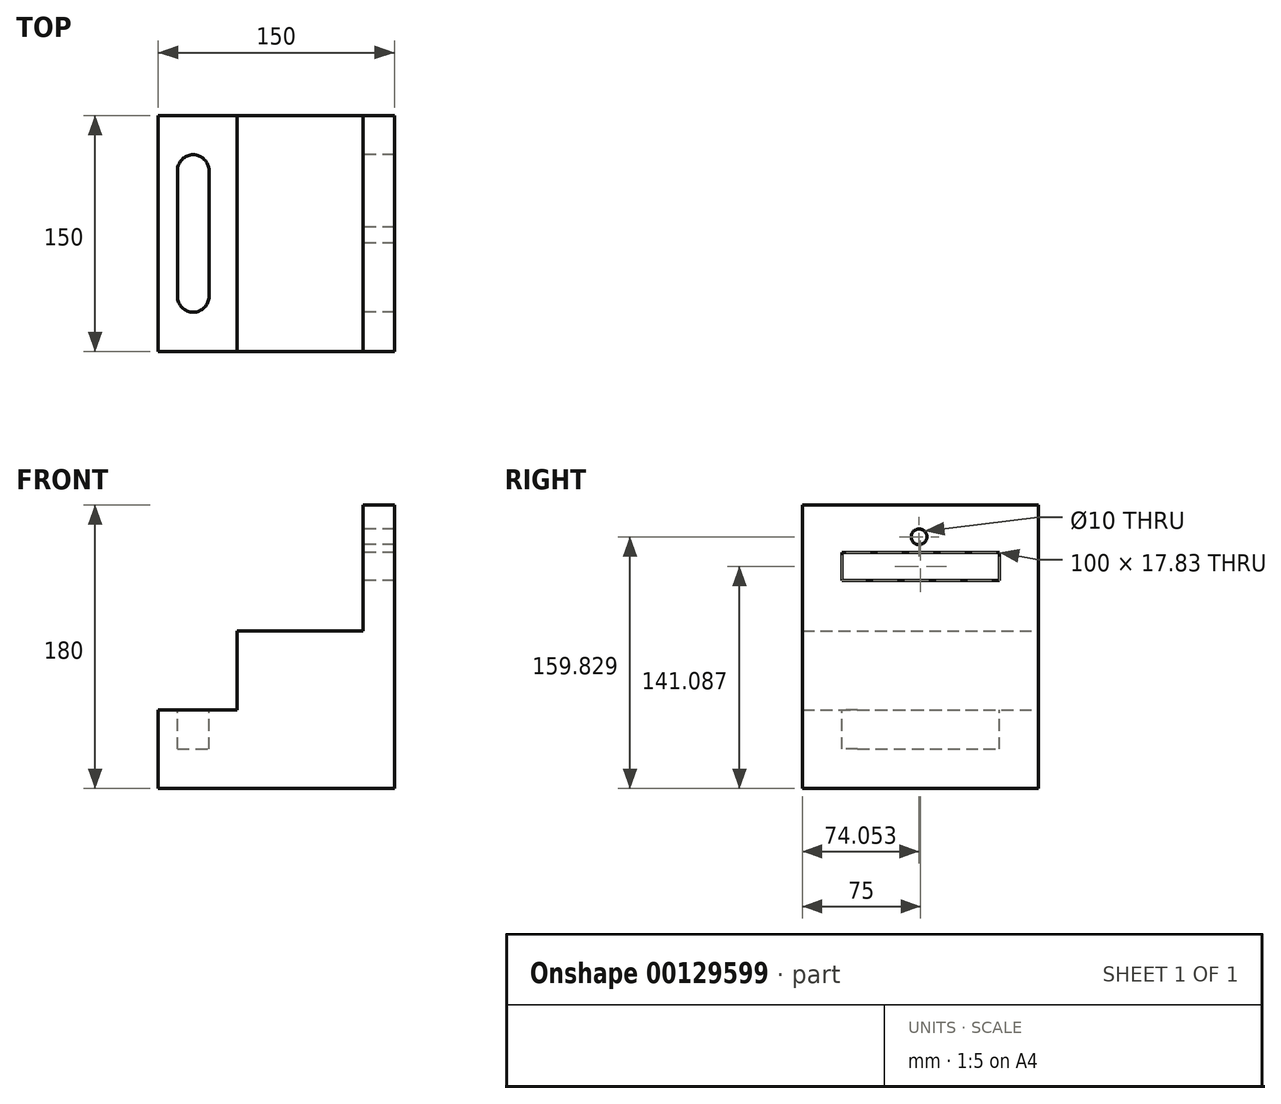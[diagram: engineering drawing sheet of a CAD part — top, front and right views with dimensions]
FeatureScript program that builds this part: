
annotation { "Feature Type Name" : "Feature", "Feature Type Description" : "" }
export const myFeature = defineFeature(function(context is Context, id is Id, definition is map)
    precondition{}
    {
        {
            var Q0;
            Q0=qCreatedBy(makeId("Front.planeOp"),FACE);
            var sketch = newSketch(context, id + "F0", { "sketchPlane" : qUnion([Q0])});
            skLineSegment(sketch, "E0.bottom", {"start": v(75, 90) * mm, "end": v(55, 90) * mm});
            skLineSegment(sketch, "E0.top", {"start": v(75, -90) * mm, "end": v(-75, -90) * mm});
            skLineSegment(sketch, "E0.left", {"start": v(75, 90) * mm, "end": v(75, -90) * mm});
            skLineSegment(sketch, "E0.right", {"start": v(-75, -40) * mm, "end": v(-75, -90) * mm});
            skPoint(sketch, "E0.middle", {"position": v(0, 0) * mm});
            skLineSegment(sketch, "E1", {"start": v(55, 90) * mm, "end": v(55, 10) * mm});
            skLineSegment(sketch, "E2", {"start": v(55, 10) * mm, "end": v(-25, 10) * mm});
            skLineSegment(sketch, "E3", {"start": v(-25, 10) * mm, "end": v(-25, -40) * mm});
            skLineSegment(sketch, "E4", {"start": v(-25, -40) * mm, "end": v(-75, -40) * mm});
            skPoint(sketch, "E5.orphan", {"position": v(-75, 90) * mm});
            skSolve(sketch);
        }
        {
            var Q0;
            Q0 = qSketchRegion(id + "F0", true);
            extrude(context, id + "F1", {"entities" : qUnion([Q0]), "depth" : 150 * mm});
        }
        {
            var Q0;
            Q0=makeQuery(id+"F1.opExtrude","SWEPT_FACE",FACE,{"disambiguationData":[OSD([sQuery(id+"F0.wireOp",EDGE,"E1")])]});
            var sketch = newSketch(context, id + "F2", { "sketchPlane" : qUnion([Q0])});
            skCircle(sketch, "E6", {"center": v(75.95, 69.83) * mm, "radius": 5 * mm});
            skSolve(sketch);
        }
        {
            var Q0;
            Q0=makeQuery(id+"F2.imprint","IMPRINT",FACE,{"disambiguationData":[TD([[makeQuery(id+"F2.imprint","IMPRINT",EDGE,{"derivedFrom":sQuery(id+"F2.wireOp",EDGE,"E6")}),1.0]])]});
            extrude(context, id + "F3", {"entities" : qUnion([Q0]), "operationType" : NewBodyOperationType.REMOVE, "endBound" : BoundingType.THROUGH_ALL, "oppositeDirection" : true, "depth" : 25.4 * mm});
        }
        {
            var Q0;
            Q0=makeQuery(id+"F1.opExtrude","SWEPT_FACE",FACE,{"disambiguationData":[OSD([sQuery(id+"F0.wireOp",EDGE,"E1")])]});
            var sketch = newSketch(context, id + "F4", { "sketchPlane" : qUnion([Q0])});
            skLineSegment(sketch, "E7.bottom", {"start": v(25, 60) * mm, "end": v(125, 60) * mm});
            skLineSegment(sketch, "E7.top", {"start": v(25, 42.17) * mm, "end": v(125, 42.17) * mm});
            skLineSegment(sketch, "E7.left", {"start": v(25, 60) * mm, "end": v(25, 42.17) * mm});
            skLineSegment(sketch, "E7.right", {"start": v(125, 60) * mm, "end": v(125, 42.17) * mm});
            skSolve(sketch);
        }
        {
            var Q0;
            Q0 = qSketchRegion(id + "F4", true);
            extrude(context, id + "F5", {"entities" : qUnion([Q0]), "operationType" : NewBodyOperationType.REMOVE, "endBound" : BoundingType.THROUGH_ALL, "oppositeDirection" : true, "depth" : 25.4 * mm});
        }
        {
            var Q0;
            Q0=makeQuery(id+"F1.opExtrude","SWEPT_FACE",FACE,{"disambiguationData":[OSD([sQuery(id+"F0.wireOp",EDGE,"E4")])]});
            var sketch = newSketch(context, id + "F6", { "sketchPlane" : qUnion([Q0])});
            skPoint(sketch, "E8", {"position": v(-75, -75) * mm});
            skLineSegment(sketch, "E9.bottom", {"start": v(-62.76, -115) * mm, "end": v(-42.76, -115) * mm});
            skLineSegment(sketch, "E9.top", {"start": v(-62.76, -35) * mm, "end": v(-42.76, -35) * mm});
            skLineSegment(sketch, "E9.left", {"start": v(-62.76, -115) * mm, "end": v(-62.76, -35) * mm});
            skLineSegment(sketch, "E9.right", {"start": v(-42.76, -115) * mm, "end": v(-42.76, -35) * mm});
            skPoint(sketch, "E9.middle", {"position": v(-52.76, -75) * mm});
            skCircle(sketch, "E10", {"center": v(-52.76, -35) * mm, "radius": 10 * mm});
            skCircle(sketch, "E11", {"center": v(-52.76, -115) * mm, "radius": 10 * mm});
            skSolve(sketch);
        }
        {
            var Q0;
            Q0 = qSketchRegion(id + "F6", true);
            extrude(context, id + "F7", {"entities" : qUnion([Q0]), "operationType" : NewBodyOperationType.REMOVE, "oppositeDirection" : true, "depth" : 25 * mm});
        }
    });
